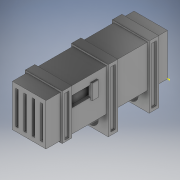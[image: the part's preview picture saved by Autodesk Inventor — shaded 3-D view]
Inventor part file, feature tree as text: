
AUTODESK INVENTOR PART (.ipt)
format: ipt  version: 2021 (Build 250183000, 183)  size: 1,630,208 bytes
history: native  units: mm
features: sketch x21, extrude x15, plane x1, emboss x1
ambient origin geometry x8: Origin, YZ Plane, XZ Plane, XY Plane, X Axis, Y Axis, Z Axis, Center Point
bodies: Solid1 (feature_tree)
feature tree (38):
  extrude  "Extrusion1"  Depth=50.8mm
  extrude  "Extrusion2"  Depth=3.742mm
  sketch  "Sketch3"  dims[d5=50.292mm d6=5.021mm]
  plane  "Work Plane1"
  extrude  "Extrusion3"  Depth=5.021mm
  sketch  "Sketch4"  dims[d7=6.604mm d8=8.704mm]
  extrude  "Extrusion4"  Depth=8.704mm
  extrude  "Extrusion5"  Depth=3.742mm
  extrude  "Extrusion6"  Depth=8.704mm
  sketch  "Sketch8"  dims[d17=100.0mm d18=0.0mm d19=94.707mm]
  extrude  "Extrusion7"  Depth=8.704mm
  sketch  "Sketch10"  dims[d22=2.54mm d23=94.707mm d24=14.463mm]
  sketch  "Sketch11"  dims[d25=68.58mm d26=14.463mm d27=2.54mm d28=2.54mm]
  extrude  "Extrusion8"  Depth=94.707mm
  extrude  "Extrusion9"  Depth=15.895mm
  extrude  "Extrusion10"  Depth=94.707mm
  sketch  "Sketch13"  dims[d31=2.54mm d32=55.88mm d33=0.0mm]
  extrude  "Extrusion11"  Depth=2.54mm
  extrude  "Extrusion12"  Depth=55.369mm
  extrude  "Extrusion13"  Depth=55.88mm TaperAngle=0.0deg
  extrude  "Extrusion14"  Depth=85.239mm
  sketch  "Sketch18"  dims[d41=4.53mm]
  sketch  "Sketch19"  dims[d42=61.42mm]
  extrude  "Extrusion15"  Depth=6.982mm
  emboss  "Emboss1"
  sketch  "Sketch1"  dims[d0=63.5mm d1=50.8mm]
  sketch  "Sketch2"  dims[d2=184.15mm d3=0.0mm d4=3.742mm]
  sketch  "Sketch5"  dims[d9=6.604mm d10=3.742mm]
  sketch  "Sketch6"  dims[d11=3.742mm d12=8.704mm]
  sketch  "Sketch7"  dims[d13=3.742mm d16=8.704mm]
  sketch  "Sketch9"  dims[d20=14.463mm d21=15.895mm]
  sketch  "Sketch12"  dims[d29=47.547mm d30=55.369mm]
  sketch  "Sketch14"  dims[d34=6.982mm d35=85.239mm]
  sketch  "Sketch15"  dims[d36=3.725mm d37=6.982mm d38=85.239mm]
  sketch  "Sketch16"  dims[d39=3.725mm]
  sketch  "Sketch17"  dims[d40=4.53mm]
  sketch  "Sketch20"  dims[d43=5.881mm]
  sketch  "Sketch21"  dims[d44=4.287mm d45=2.54mm d46=0.0mm d48=9.417mm d49=14.937mm d50=9.819mm d51=22.975mm d52=1.905mm d53=0.0mm d54=13.021mm d55=16.131mm d56=6.926mm d57=0.0mm d58=16.131mm d59=1.905mm d60=9.417mm d61=0.0mm d62=27.142mm d63=14.282mm d64=24.181mm d65=24.181mm d66=14.282mm d67=27.142mm d68=30.0mm d69=0.0mm d70=30.0mm d71=0.0mm d72=0.127mm d73=0.684mm d74=24.765mm d75=500.0mm d76=0.0mm d77=31.015mm d80=9.819mm d81=9.417mm d82=22.975mm d83=5.021mm d84=0.0mm d85=16.131mm d86=13.021mm d87=5.021mm d88=0.0mm d89=16.131mm d90=1.905mm d91=9.417mm d92=0.0mm d93=10.502mm d94=10.502mm d95=6.507mm d96=21.312mm d97=6.507mm d98=10.502mm d99=10.502mm d100=21.312mm d101=2.54mm d102=0.0mm d103=5.881mm d104=61.42mm d105=4.62mm d106=4.295mm d107=6.982mm d108=85.239mm d109=4.938mm d110=3.725mm d111=6.982mm d112=85.239mm d113=4.938mm d114=3.725mm d115=2.54mm d116=0.0mm d117=2.0mm d118=0.0mm d78=0.872665mm]
